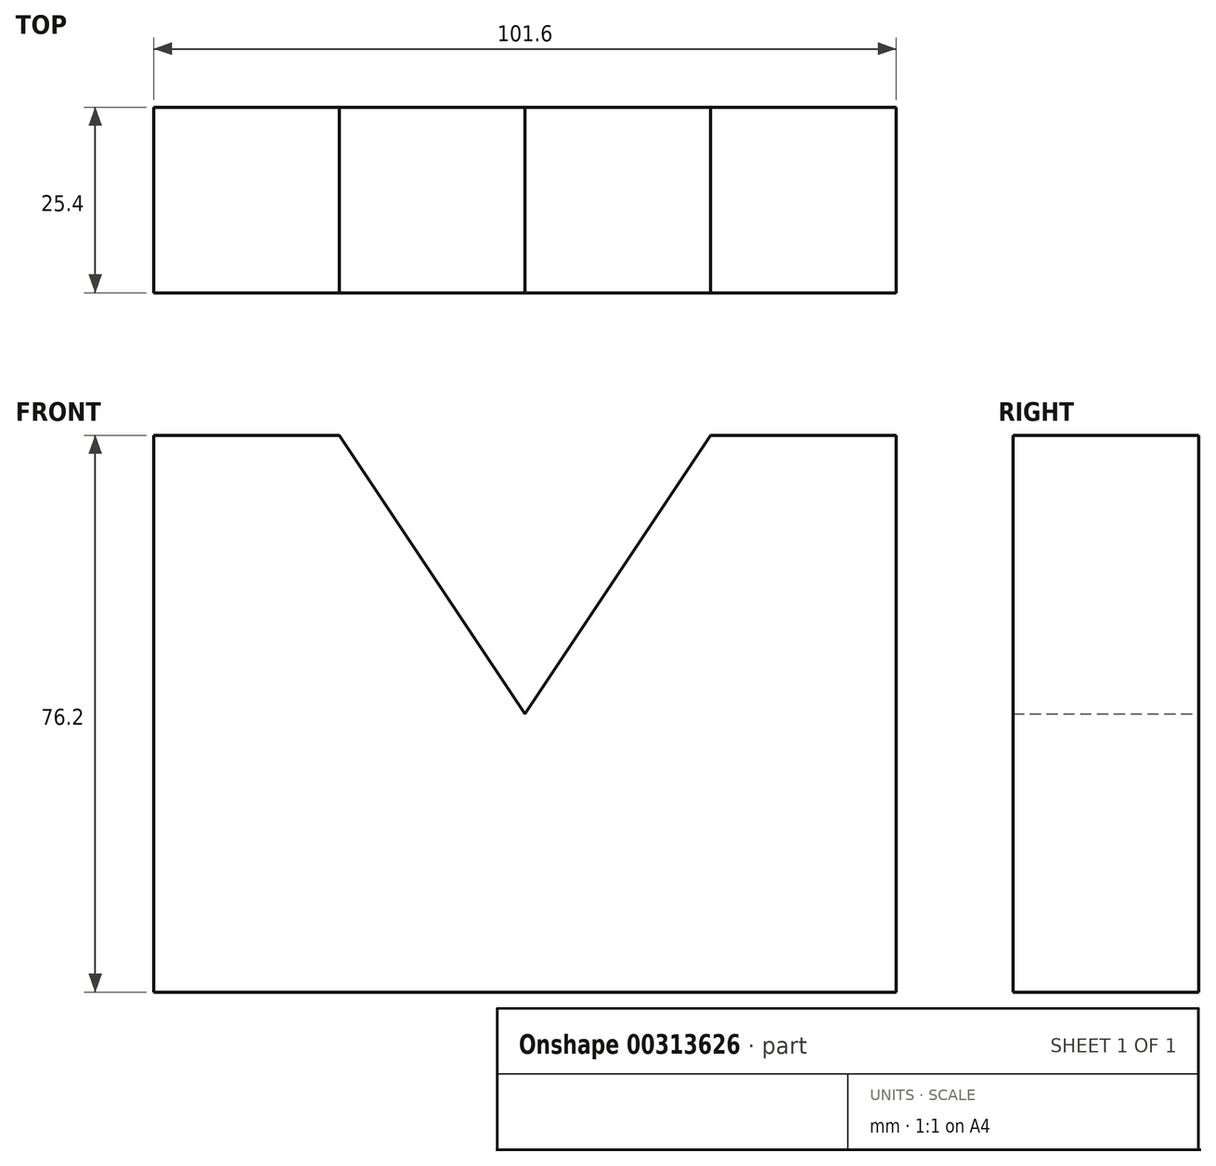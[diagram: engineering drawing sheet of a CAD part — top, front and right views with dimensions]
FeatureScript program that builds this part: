
annotation { "Feature Type Name" : "Feature", "Feature Type Description" : "" }
export const myFeature = defineFeature(function(context is Context, id is Id, definition is map)
    precondition{}
    {
        {
            var Q0;
            Q0=qCreatedBy(makeId("Front.planeOp"),FACE);
            var sketch = newSketch(context, id + "F0", { "sketchPlane" : qUnion([Q0])});
            skLineSegment(sketch, "E0", {"start": v(-62.35, -48.77) * mm, "end": v(39.25, -48.77) * mm});
            skLineSegment(sketch, "E1", {"start": v(-62.35, -48.77) * mm, "end": v(-62.35, 27.43) * mm});
            skLineSegment(sketch, "E2", {"start": v(-62.35, 27.43) * mm, "end": v(-36.95, 27.43) * mm});
            skLineSegment(sketch, "E3", {"start": v(39.25, -48.77) * mm, "end": v(39.25, 27.43) * mm});
            skLineSegment(sketch, "E4", {"start": v(39.25, 27.43) * mm, "end": v(13.85, 27.43) * mm});
            skLineSegment(sketch, "E5", {"start": v(-36.95, 27.43) * mm, "end": v(-11.55, -10.67) * mm});
            skLineSegment(sketch, "E6", {"start": v(13.85, 27.43) * mm, "end": v(-11.55, -10.67) * mm});
            skSolve(sketch);
        }
        {
            var Q0;
            Q0 = qSketchRegion(id + "F0", true);
            extrude(context, id + "F1", {"entities" : qUnion([Q0]), "depth" : 25.4 * mm});
        }
    });
